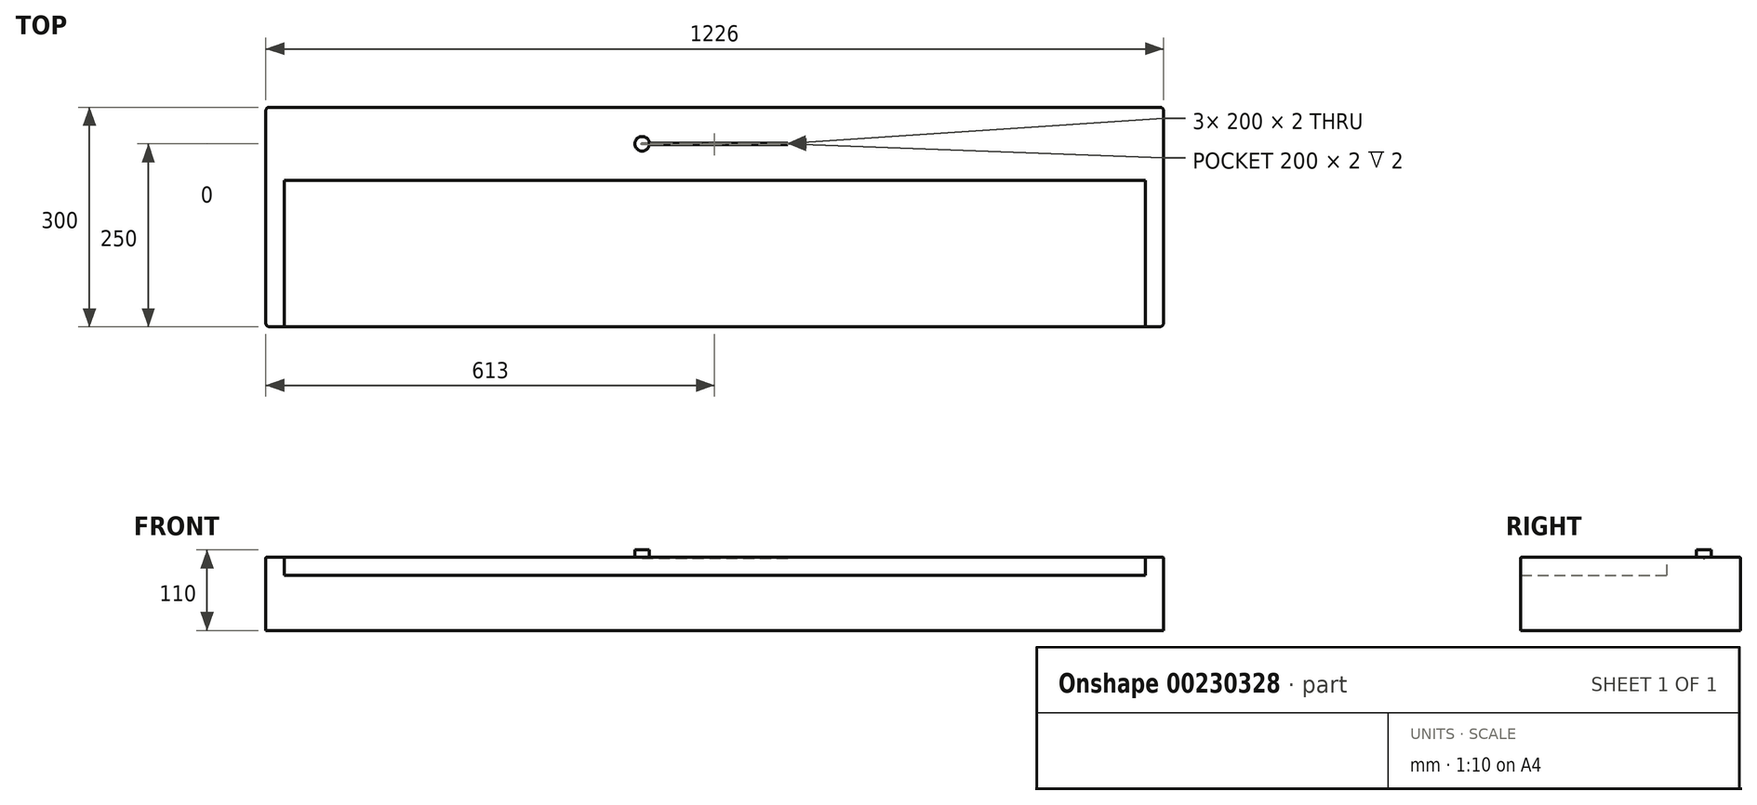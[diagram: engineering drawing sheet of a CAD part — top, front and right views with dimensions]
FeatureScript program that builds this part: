
annotation { "Feature Type Name" : "Feature", "Feature Type Description" : "" }
export const myFeature = defineFeature(function(context is Context, id is Id, definition is map)
    precondition{}
    {
        {
            var Q0;
            Q0=qCreatedBy(makeId("Top.planeOp"),FACE);
            var sketch = newSketch(context, id + "F0", { "sketchPlane" : qUnion([Q0])});
            skLineSegment(sketch, "E0.bottom", {"start": v(613, -150) * mm, "end": v(-613, -150) * mm});
            skLineSegment(sketch, "E0.top", {"start": v(613, 150) * mm, "end": v(-613, 150) * mm});
            skLineSegment(sketch, "E0.left", {"start": v(613, -150) * mm, "end": v(613, 150) * mm});
            skLineSegment(sketch, "E0.right", {"start": v(-613, -150) * mm, "end": v(-613, 150) * mm});
            skPoint(sketch, "E0.middle", {"position": v(0, 0) * mm});
            skSolve(sketch);
        }
        {
            var Q0;
            Q0 = qSketchRegion(id + "F0", true);
            extrude(context, id + "F1", {"entities" : qUnion([Q0]), "depth" : 100 * mm});
        }
        {
            var Q0;
            Q0=makeQuery(id+"F1.opExtrude","CAP_FACE",FACE,{"disambiguationData":[OSD([sQuery(id+"F0.wireOp",EDGE,"E0.bottom"),sQuery(id+"F0.wireOp",EDGE,"E0.top"),sQuery(id+"F0.wireOp",EDGE,"E0.left"),sQuery(id+"F0.wireOp",EDGE,"E0.right")])],"isStart":false});
            var sketch = newSketch(context, id + "F2", { "sketchPlane" : qUnion([Q0])});
            skLineSegment(sketch, "E1.bottom", {"start": v(-588, -150) * mm, "end": v(588, -150) * mm});
            skLineSegment(sketch, "E1.top", {"start": v(-588, 50) * mm, "end": v(588, 50) * mm});
            skLineSegment(sketch, "E1.left", {"start": v(-588, -150) * mm, "end": v(-588, 50) * mm});
            skLineSegment(sketch, "E1.right", {"start": v(588, -150) * mm, "end": v(588, 50) * mm});
            skSolve(sketch);
        }
        {
            var Q0;
            Q0 = qSketchRegion(id + "F2", true);
            extrude(context, id + "F3", {"entities" : qUnion([Q0]), "operationType" : NewBodyOperationType.REMOVE, "oppositeDirection" : true, "depth" : 25 * mm});
        }
        {
            var Q0;
            Q0=makeQuery(id+"F1.opExtrude","CAP_FACE",FACE,{"disambiguationData":[OSD([sQuery(id+"F0.wireOp",EDGE,"E0.bottom"),sQuery(id+"F0.wireOp",EDGE,"E0.top"),sQuery(id+"F0.wireOp",EDGE,"E0.left"),sQuery(id+"F0.wireOp",EDGE,"E0.right")])],"isStart":false});
            var sketch = newSketch(context, id + "F4", { "sketchPlane" : qUnion([Q0])});
            skLineSegment(sketch, "E2.bottom", {"start": v(100, 99) * mm, "end": v(-100, 99) * mm});
            skLineSegment(sketch, "E2.top", {"start": v(100, 101) * mm, "end": v(-100, 101) * mm});
            skLineSegment(sketch, "E2.left", {"start": v(100, 99) * mm, "end": v(100, 101) * mm});
            skLineSegment(sketch, "E2.right", {"start": v(-100, 99) * mm, "end": v(-100, 101) * mm});
            skPoint(sketch, "E2.middle", {"position": v(0, 100) * mm});
            skSolve(sketch);
        }
        {
            var Q0;
            Q0 = qSketchRegion(id + "F4", true);
            extrude(context, id + "F5", {"entities" : qUnion([Q0]), "operationType" : NewBodyOperationType.REMOVE, "oppositeDirection" : true, "depth" : 2 * mm});
        }
        {
            var Q0;
            Q0=makeQuery(id+"F1.opExtrude","CAP_FACE",FACE,{"disambiguationData":[OSD([sQuery(id+"F0.wireOp",EDGE,"E0.bottom"),sQuery(id+"F0.wireOp",EDGE,"E0.top"),sQuery(id+"F0.wireOp",EDGE,"E0.left"),sQuery(id+"F0.wireOp",EDGE,"E0.right")])],"isStart":false});
            var sketch = newSketch(context, id + "F6", { "sketchPlane" : qUnion([Q0])});
            skCircle(sketch, "E3", {"center": v(-99, 100) * mm, "radius": 10 * mm});
            skSolve(sketch);
        }
        {
            var Q0;
            Q0 = qSketchRegion(id + "F6", true);
            extrude(context, id + "F7", {"entities" : qUnion([Q0]), "depth" : 10 * mm});
        }
        {
            var Q0;
            Q0=makeQuery(id+"F1.opExtrude","SWEPT_EDGE",EDGE,{"disambiguationData":[OSD([sQuery(id+"F0.wireOp",EDGE,"E0.top"),sQuery(id+"F0.wireOp",EDGE,"E0.right")])]});
            var Q1;
            Q1=makeQuery(id+"F1.opExtrude","SWEPT_EDGE",EDGE,{"disambiguationData":[OSD([sQuery(id+"F0.wireOp",EDGE,"E0.bottom"),sQuery(id+"F0.wireOp",EDGE,"E0.right")])]});
            var Q2;
            Q2=makeQuery(id+"F1.opExtrude","SWEPT_EDGE",EDGE,{"disambiguationData":[OSD([sQuery(id+"F0.wireOp",EDGE,"E0.bottom"),sQuery(id+"F0.wireOp",EDGE,"E0.left")])]});
            var Q3;
            Q3=makeQuery(id+"F1.opExtrude","SWEPT_EDGE",EDGE,{"disambiguationData":[OSD([sQuery(id+"F0.wireOp",EDGE,"E0.top"),sQuery(id+"F0.wireOp",EDGE,"E0.left")])]});
            fillet(context, id + "F8", {"entities" : qUnion([Q0, Q1, Q2, Q3]), "radius" : 5 * mm, "tangentPropagation" : true, "allowEdgeOverflow" : false});
        }
        {
            var Q0;
            Q0=makeQuery(id+"F1.opExtrude","CAP_EDGE",EDGE,{"disambiguationData":[OSD([sQuery(id+"F0.wireOp",EDGE,"E0.right")])],"isStart":false});
            fillet(context, id + "F9", {"entities" : qUnion([Q0]), "radius" : 1 * mm, "tangentPropagation" : true, "allowEdgeOverflow" : false});
        }
    });
